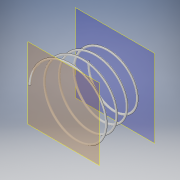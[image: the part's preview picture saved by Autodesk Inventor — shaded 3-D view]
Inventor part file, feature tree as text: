
AUTODESK INVENTOR PART (.ipt)
format: ipt  version: 2017 (Build 210142000, 142)  size: 202,240 bytes
history: native  units: in
note: dims shown in document units (in); Inventor stores cm internally (conversion verified against a paired STEP export)
features: plane x2, helix x1, sketch x1
ambient origin geometry x8: Origin, YZ Plane, XZ Plane, XY Plane, X Axis, Y Axis, Z Axis, Center Point
bodies: Solid1 (feature_tree)
feature tree (4):
  plane  "Work Plane1"
  plane  "Work Plane2"
  helix  "Coil1"  [1 undecoded]
  sketch  "Sketch1"  dims[d2=0.2953in d3=0.0197in d5=0.3937in d6=0.5512in d7=1.5748in d8=0.0687in d9=90.0deg d10=90.0deg d11=0.0in d12=0.0in]
note: 1 required parameter value undecoded (feature->parameter linkage not recoverable at this tier; creation-order binding heuristic only, values carry confidence <= 0.55)
